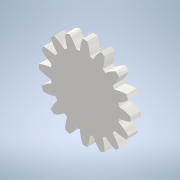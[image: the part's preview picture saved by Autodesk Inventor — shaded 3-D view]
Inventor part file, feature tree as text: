
AUTODESK INVENTOR PART (.ipt)
format: ipt  version: 2021 (Build 250183000, 183)  size: 205,824 bytes
history: native  units: mm (DEFAULTED — no unit token found)
features: plane x3, other x3, sketch x2, extrude x1
ambient origin geometry x8: Origin, YZ Plane, XZ Plane, XY Plane, X Axis, Y Axis, Z Axis, Center Point
bodies: Solid1 (feature_tree)
feature tree (9):
  extrude  "Extrusion1"  Depth=20.0mm TaperAngle=0.0deg
  plane  "Work Plane2"
  plane  "Work Plane8"
  plane  "Work Plane9"
  other  "Engrenage cylindrique"
  sketch  "Sketch1"  dims[d0=63.0mm d1=20.0mm d2=0.0mm]
  sketch  "Sketch2"  dims[d3=56.0mm d4=18.0mm d5=0.0mm d16=63.0mm d17=0.0mm d34=1.963495mm d39=0.0mm d41=0.0mm d43=63.0mm d46=63.0mm d47=0.0mm d48=0.0mm]
  other  "Srf1"
  other  "Diamètre primitif"
